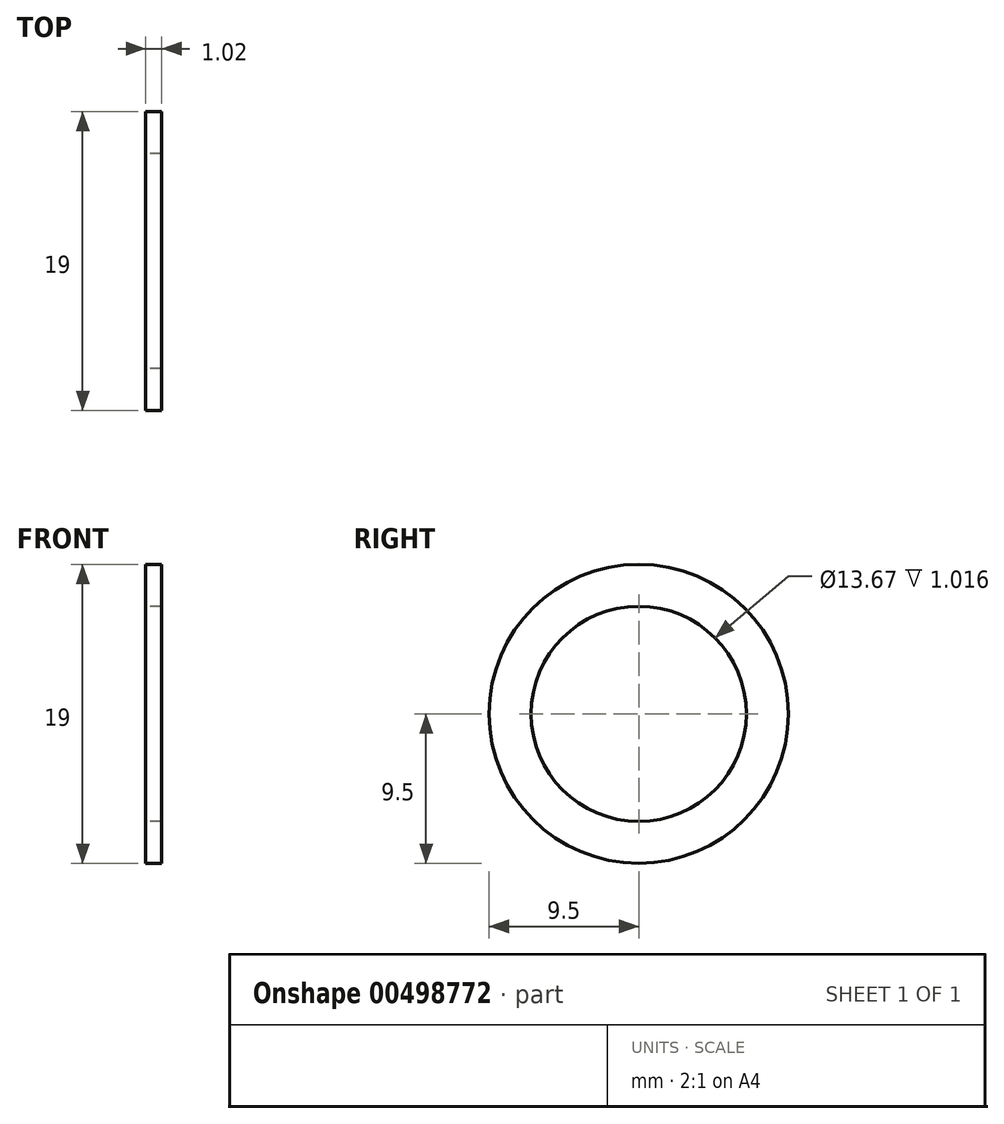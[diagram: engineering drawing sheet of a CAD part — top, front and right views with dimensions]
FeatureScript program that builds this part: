
annotation { "Feature Type Name" : "Feature", "Feature Type Description" : "" }
export const myFeature = defineFeature(function(context is Context, id is Id, definition is map)
    precondition{}
    {
        {
            var Q0;
            Q0=qCreatedBy(makeId("Right.planeOp"),FACE);
            var sketch = newSketch(context, id + "F0", { "sketchPlane" : qUnion([Q0])});
            skCircle(sketch, "E0", {"center": v(0, 0) * mm, "radius": 9.5 * mm});
            skLineSegment(sketch, "E1", {"start": v(0, 9.5) * mm, "end": v(0, 6.83) * mm});
            skLineSegment(sketch, "E2", {"start": v(0, -9.5) * mm, "end": v(0, -6.83) * mm});
            skLineSegment(sketch, "E3", {"start": v(-9.5, 0) * mm, "end": v(-6.83, 0) * mm});
            skLineSegment(sketch, "E4", {"start": v(9.5, 0) * mm, "end": v(6.83, 0) * mm});
            skCircle(sketch, "E5", {"center": v(0, 0) * mm, "radius": 6.83 * mm});
            skSolve(sketch);
        }
        {
            var Q0;
            {var subQ0=sQuery(id+"F0.wireOp",EDGE,"E1");Q0=makeQuery(id+"F0.imprint","IMPRINT",FACE,{"disambiguationData":[TD([[makeQuery(id+"F0.imprint","IMPRINT",EDGE,{"derivedFrom":subQ0}),-1.0]])]});}
            var Q1;
            {var subQ0=sQuery(id+"F0.wireOp",EDGE,"E1");Q1=makeQuery(id+"F0.imprint","IMPRINT",FACE,{"disambiguationData":[TD([[makeQuery(id+"F0.imprint","IMPRINT",EDGE,{"derivedFrom":subQ0}),1.0]])]});}
            var Q2;
            {var subQ0=sQuery(id+"F0.wireOp",EDGE,"E2");Q2=makeQuery(id+"F0.imprint","IMPRINT",FACE,{"disambiguationData":[TD([[makeQuery(id+"F0.imprint","IMPRINT",EDGE,{"derivedFrom":subQ0}),-1.0]])]});}
            var Q3;
            {var subQ0=sQuery(id+"F0.wireOp",EDGE,"E2");Q3=makeQuery(id+"F0.imprint","IMPRINT",FACE,{"disambiguationData":[TD([[makeQuery(id+"F0.imprint","IMPRINT",EDGE,{"derivedFrom":subQ0}),1.0]])]});}
            extrude(context, id + "F1", {"entities" : qUnion([Q0, Q1, Q2, Q3]), "depth" : 1.02 * mm});
        }
    });
